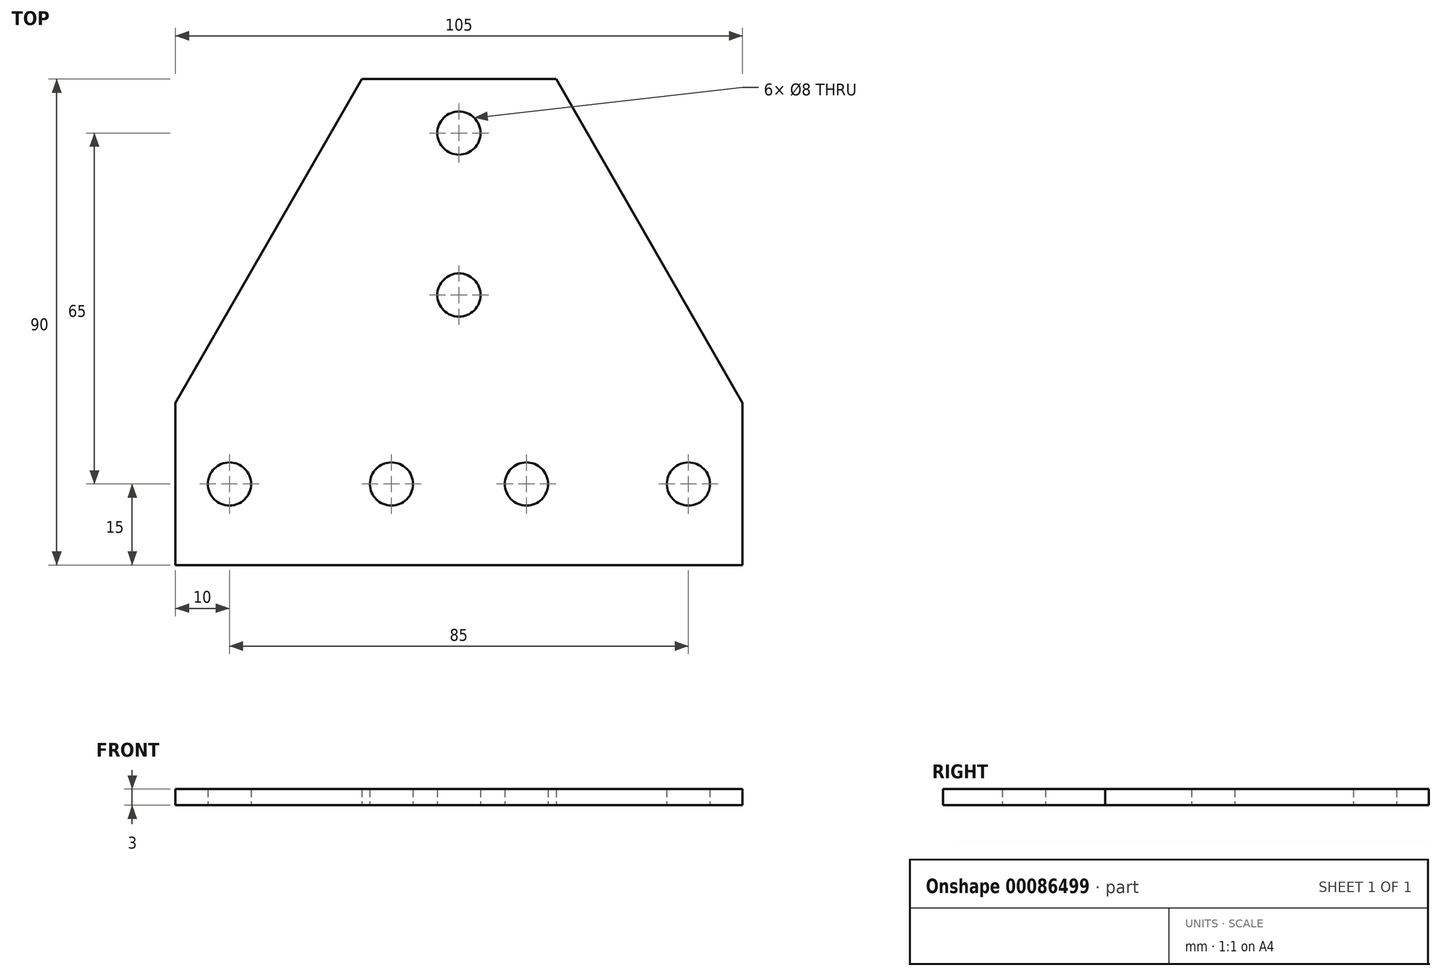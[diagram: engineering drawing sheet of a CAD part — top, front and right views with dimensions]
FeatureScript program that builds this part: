
annotation { "Feature Type Name" : "Feature", "Feature Type Description" : "" }
export const myFeature = defineFeature(function(context is Context, id is Id, definition is map)
    precondition{}
    {
        {
            var Q0;
            Q0=qCreatedBy(makeId("Top.planeOp"),FACE);
            var sketch = newSketch(context, id + "F0", { "sketchPlane" : qUnion([Q0])});
            skLineSegment(sketch, "E0", {"start": v(-52.5, -40) * mm, "end": v(-52.5, -10) * mm});
            skLineSegment(sketch, "E1", {"start": v(-52.5, -10) * mm, "end": v(-18, 50) * mm});
            skLineSegment(sketch, "E2", {"start": v(-18, 50) * mm, "end": v(18, 50) * mm});
            skLineSegment(sketch, "E3", {"start": v(18, 50) * mm, "end": v(52.5, -10) * mm});
            skLineSegment(sketch, "E4", {"start": v(52.5, -10) * mm, "end": v(52.5, -40) * mm});
            skLineSegment(sketch, "E5", {"start": v(52.5, -40) * mm, "end": v(-52.5, -40) * mm});
            skPoint(sketch, "E6", {"position": v(0, 50) * mm});
            skPoint(sketch, "E7", {"position": v(0, -40) * mm});
            skCircle(sketch, "E8", {"center": v(-42.5, -25) * mm, "radius": 4 * mm});
            skCircle(sketch, "E9", {"center": v(42.5, -25) * mm, "radius": 4 * mm});
            skCircle(sketch, "E10", {"center": v(12.5, -25) * mm, "radius": 4 * mm});
            skCircle(sketch, "E11", {"center": v(-12.5, -25) * mm, "radius": 4 * mm});
            skLineSegment(sketch, "E12", {"start": v(52.5, -25) * mm, "end": v(-52.5, -25) * mm, "construction": true});
            skCircle(sketch, "E13", {"center": v(0, 40) * mm, "radius": 4 * mm});
            skCircle(sketch, "E14", {"center": v(0, 10) * mm, "radius": 4 * mm});
            skSolve(sketch);
        }
        {
            var Q0;
            Q0=makeQuery(id+"F0.imprint","IMPRINT",FACE,{"disambiguationData":[TD([[makeQuery(id+"F0.imprint","IMPRINT",EDGE,{"derivedFrom":sQuery(id+"F0.wireOp",EDGE,"E0")}),-1.0]])]});
            extrude(context, id + "F1", {"entities" : qUnion([Q0]), "depth" : 3 * mm});
        }
    });
